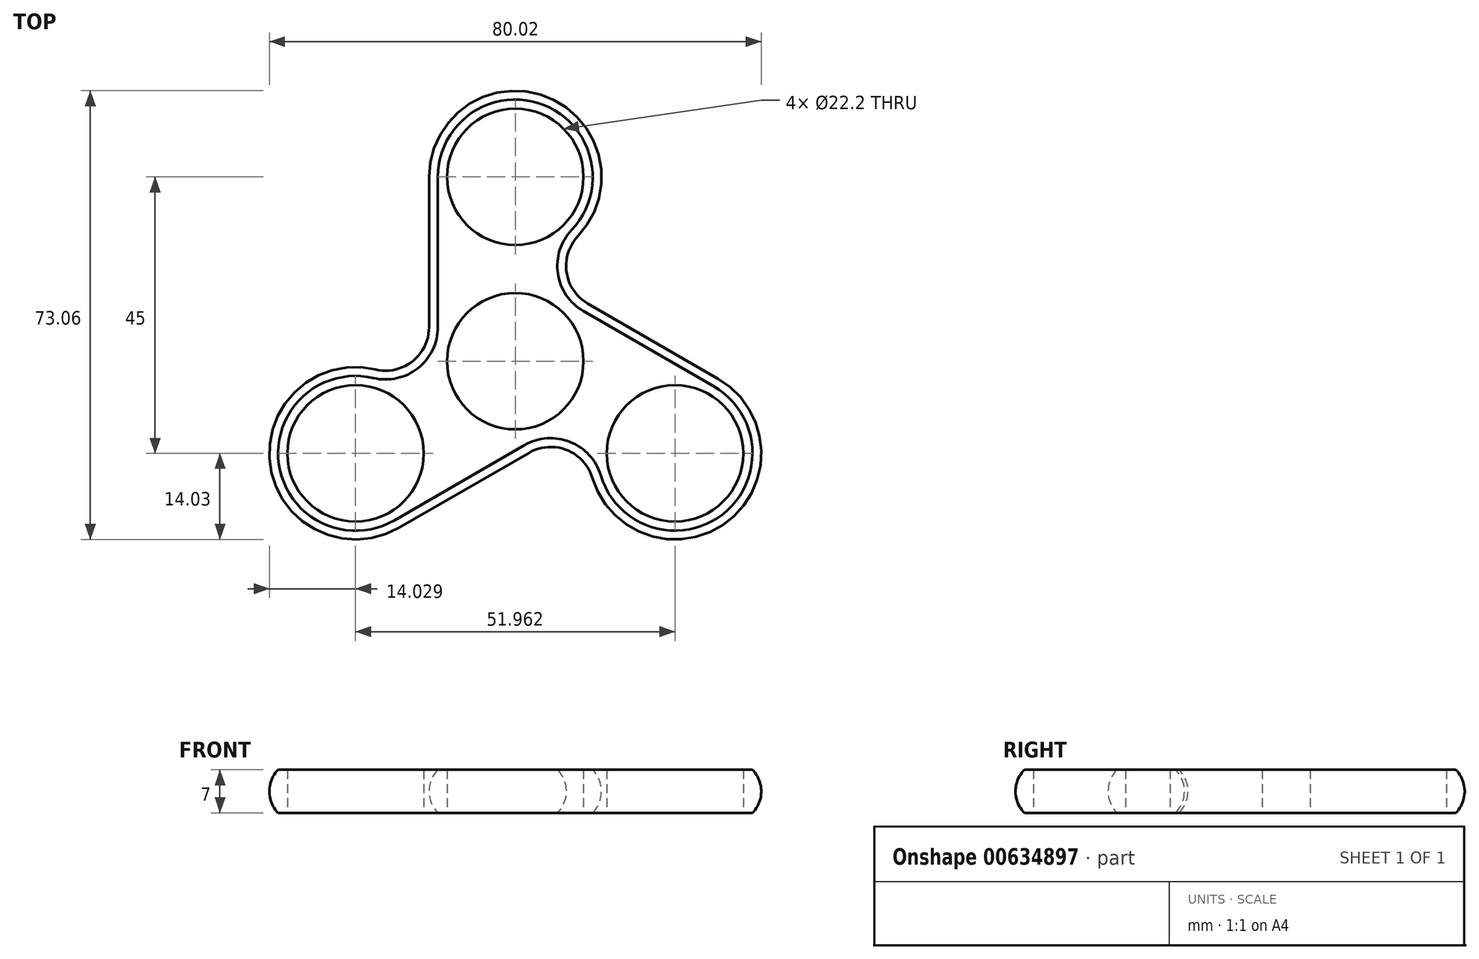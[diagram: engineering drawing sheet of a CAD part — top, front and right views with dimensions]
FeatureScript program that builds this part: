
annotation { "Feature Type Name" : "Feature", "Feature Type Description" : "" }
export const myFeature = defineFeature(function(context is Context, id is Id, definition is map)
    precondition{}
    {
        {
            var Q0;
            Q0=qCreatedBy(makeId("Top.planeOp"),FACE);
            var sketch = newSketch(context, id + "F0", { "sketchPlane" : qUnion([Q0])});
            skCircle(sketch, "E0", {"center": v(0, 0) * mm, "radius": 11.1 * mm});
            skCircle(sketch, "E1", {"center": v(0, 30) * mm, "radius": 11.1 * mm});
            skCircle(sketch, "E2.1.0", {"center": v(-25.98, -15) * mm, "radius": 11.1 * mm});
            skCircle(sketch, "E2.2.0", {"center": v(25.98, -15) * mm, "radius": 11.1 * mm});
            skArc(sketch, "E3.0", {"start": v(6.07, 15.09) * mm, "mid": v(8.99, 43.36) * mm, "end": v(-16.1, 30) * mm});
            skArc(sketch, "E4.1.0", {"start": v(-16.1, -2.29) * mm, "mid": v(-42.04, -13.9) * mm, "end": v(-17.93, -28.94) * mm});
            skArc(sketch, "E4.2.0", {"start": v(10.03, -12.8) * mm, "mid": v(33.06, -29.46) * mm, "end": v(34.03, -1.06) * mm});
            skLineSegment(sketch, "E5", {"start": v(-16.1, 30) * mm, "end": v(-16.1, -2.29) * mm});
            skLineSegment(sketch, "E6.1.0", {"start": v(-17.93, -28.94) * mm, "end": v(10.03, -12.8) * mm});
            skLineSegment(sketch, "E6.2.0", {"start": v(34.03, -1.06) * mm, "end": v(6.07, 15.09) * mm});
            skSolve(sketch);
        }
        {
            var Q0;
            Q0=makeQuery(id+"F0.imprint","IMPRINT",FACE,{"disambiguationData":[TD([[makeQuery(id+"F0.imprint","IMPRINT",EDGE,{"derivedFrom":sQuery(id+"F0.wireOp",EDGE,"E0")}),-1.0]])]});
            extrude(context, id + "F1", {"entities" : qUnion([Q0]), "depth" : 7 * mm, "offsetDistance" : 25 * mm});
        }
        {
            var Q0;
            Q0=makeQuery(id+"F1.opExtrude","SWEPT_EDGE",EDGE,{"disambiguationData":[OSD([sQuery(id+"F0.wireOp",EDGE,"E3.0"),sQuery(id+"F0.wireOp",EDGE,"E6.2.0")])]});
            var Q1;
            Q1=makeQuery(id+"F1.opExtrude","SWEPT_EDGE",EDGE,{"disambiguationData":[OSD([sQuery(id+"F0.wireOp",EDGE,"E4.1.0"),sQuery(id+"F0.wireOp",EDGE,"E5")])]});
            var Q2;
            Q2=makeQuery(id+"F1.opExtrude","SWEPT_EDGE",EDGE,{"disambiguationData":[OSD([sQuery(id+"F0.wireOp",EDGE,"E4.2.0"),sQuery(id+"F0.wireOp",EDGE,"E6.1.0")])]});
            fillet(context, id + "F2", {"entities" : qUnion([Q0, Q1, Q2]), "radius" : 5 * mm, "tangentPropagation" : true, "allowEdgeOverflow" : false});
        }
        {
            var Q0;
            Q0=makeQuery(id+"F1.opExtrude","CAP_EDGE",EDGE,{"disambiguationData":[OSD([sQuery(id+"F0.wireOp",EDGE,"E4.1.0")])],"isStart":false});
            chamfer(context, id + "F3", {"entities" : qUnion([Q0]), "width" : 3.5 * mm, "tangentPropagation" : true});
        }
        {
            var Q0;
            Q0=makeQuery(id+"F1.opExtrude","CAP_EDGE",EDGE,{"disambiguationData":[OSD([sQuery(id+"F0.wireOp",EDGE,"E4.1.0")])],"isStart":true});
            chamfer(context, id + "F4", {"entities" : qUnion([Q0]), "width" : 3.5 * mm, "tangentPropagation" : true});
        }
        {
            var Q0;
            {var subQ0=sQuery(id+"F0.wireOp",EDGE,"E6.1.0");Q0=makeQuery(id+"F4.opChamfer","BLEND_EDGE",EDGE,{"blendedFrom":[makeQuery(id+"F1.opExtrude","CAP_EDGE",EDGE,{"disambiguationData":[OSD([subQ0])],"isStart":true}),makeQuery(id+"F3.opChamfer","BLEND_FACE",FACE,{"disambiguationData":[OSD([subQ0])]})],"blendedInto":[makeQuery(id+"F3.opChamfer","BLEND_FACE",FACE,{"disambiguationData":[OSD([subQ0])]})]});}
            fillet(context, id + "F5", {"entities" : qUnion([Q0]), "radius" : 5 * mm, "tangentPropagation" : true, "allowEdgeOverflow" : false});
        }
    });
